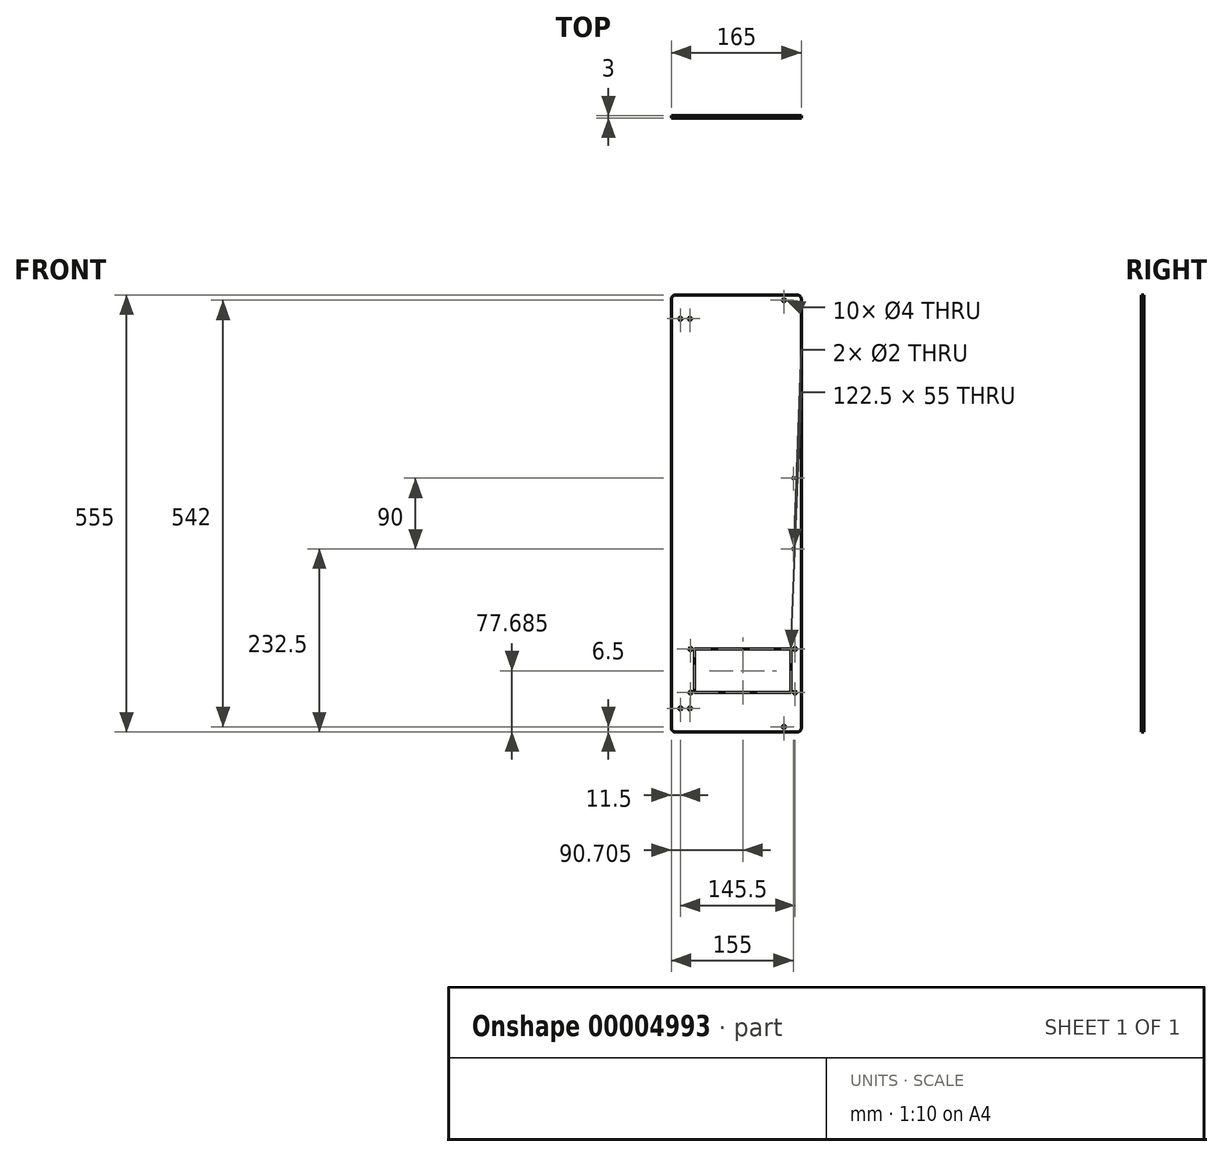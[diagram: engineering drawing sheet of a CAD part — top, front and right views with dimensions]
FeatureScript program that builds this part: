
annotation { "Feature Type Name" : "Feature", "Feature Type Description" : "" }
export const myFeature = defineFeature(function(context is Context, id is Id, definition is map)
    precondition{}
    {
        {
            var Q0;
            Q0=qCreatedBy(makeId("Front.planeOp"),FACE);
            var sketch = newSketch(context, id + "F0", { "sketchPlane" : qUnion([Q0])});
            skLineSegment(sketch, "E0.rect.bottom", {"start": v(82.5, 277.5) * mm, "end": v(-82.5, 277.5) * mm});
            skLineSegment(sketch, "E0.rect.top", {"start": v(82.5, -277.5) * mm, "end": v(-82.5, -277.5) * mm});
            skLineSegment(sketch, "E0.rect.left", {"start": v(82.5, 277.5) * mm, "end": v(82.5, -277.5) * mm});
            skLineSegment(sketch, "E0.rect.right", {"start": v(-82.5, 277.5) * mm, "end": v(-82.5, -277.5) * mm});
            skPoint(sketch, "E0.rect.middle", {"position": v(0, 0) * mm});
            skLineSegment(sketch, "E1", {"start": v(0, 277.5) * mm, "end": v(0, -277.5) * mm, "construction": true});
            skLineSegment(sketch, "E2", {"start": v(0, 0) * mm, "end": v(82.5, 0) * mm, "construction": true});
            skCircle(sketch, "E3", {"center": v(80.17, 273.25) * mm, "radius": 1.5 * mm, "construction": true});
            skCircle(sketch, "E4.0.MirrorC", {"center": v(80.17, -273.25) * mm, "radius": 1.5 * mm, "construction": true});
            skCircle(sketch, "E5.0.MirrorC", {"center": v(-80.17, -273.25) * mm, "radius": 1.5 * mm, "construction": true});
            skCircle(sketch, "E5.1.MirrorC", {"center": v(-80.17, 273.25) * mm, "radius": 1.5 * mm, "construction": true});
            skSolve(sketch);
        }
        {
            var Q0;
            Q0=qSketchRegion(id+"F0",true);
            extrude(context, id + "F1", {"entities" : qUnion([Q0]), "depth" : 3 * mm});
        }
        {
            var Q0;
            Q0=makeQuery(id+"F1.opExtrude","SWEPT_EDGE",EDGE,{"disambiguationData":[OSD([sQuery(id+"F0.wireOp",EDGE,"E0.rect.bottom"),sQuery(id+"F0.wireOp",EDGE,"E0.rect.left")])]});
            var Q1;
            Q1=makeQuery(id+"F1.opExtrude","SWEPT_EDGE",EDGE,{"disambiguationData":[OSD([sQuery(id+"F0.wireOp",EDGE,"E0.rect.bottom"),sQuery(id+"F0.wireOp",EDGE,"E0.rect.right")])]});
            var Q2;
            Q2=makeQuery(id+"F1.opExtrude","SWEPT_EDGE",EDGE,{"disambiguationData":[OSD([sQuery(id+"F0.wireOp",EDGE,"E0.rect.top"),sQuery(id+"F0.wireOp",EDGE,"E0.rect.left")])]});
            var Q3;
            Q3=makeQuery(id+"F1.opExtrude","SWEPT_EDGE",EDGE,{"disambiguationData":[OSD([sQuery(id+"F0.wireOp",EDGE,"E0.rect.top"),sQuery(id+"F0.wireOp",EDGE,"E0.rect.right")])]});
            fillet(context, id + "F2", {"entities" : qUnion([Q0, Q1, Q2, Q3]), "radius" : 5 * mm, "tangentPropagation" : true, "allowEdgeOverflow" : false});
        }
        {
            var Q0;
            Q0=makeQuery(id+"F1.opExtrude","CAP_FACE",FACE,{"disambiguationData":[OSD([sQuery(id+"F0.wireOp",EDGE,"E0.rect.bottom"),sQuery(id+"F0.wireOp",EDGE,"E0.rect.top"),sQuery(id+"F0.wireOp",EDGE,"E0.rect.left"),sQuery(id+"F0.wireOp",EDGE,"E0.rect.right")])],"isStart":false});
            var sketch = newSketch(context, id + "F3", { "sketchPlane" : qUnion([Q0])});
            skLineSegment(sketch, "E6", {"start": v(-82.5, 0) * mm, "end": v(82.5, 0) * mm, "construction": true});
            skLineSegment(sketch, "E7", {"start": v(-82.5, 247.5) * mm, "end": v(82.5, 247.5) * mm, "construction": true});
            skCircle(sketch, "E8", {"center": v(-71, 247.5) * mm, "radius": 2 * mm});
            skCircle(sketch, "E9", {"center": v(-59, 247.5) * mm, "radius": 2 * mm});
            skCircle(sketch, "E10.0.MirrorC", {"center": v(-59, -247.5) * mm, "radius": 2 * mm});
            skCircle(sketch, "E10.1.MirrorC", {"center": v(-71, -247.5) * mm, "radius": 2 * mm});
            skSolve(sketch);
        }
        {
            var Q0;
            Q0=qSketchRegion(id+"F3",true);
            extrude(context, id + "F4", {"entities" : qUnion([Q0]), "operationType" : NewBodyOperationType.REMOVE, "endBound" : BoundingType.THROUGH_ALL, "oppositeDirection" : true, "depth" : 25 * mm});
        }
        {
            var Q0;
            Q0=makeQuery(id+"F1.opExtrude","CAP_FACE",FACE,{"disambiguationData":[OSD([sQuery(id+"F0.wireOp",EDGE,"E0.rect.bottom"),sQuery(id+"F0.wireOp",EDGE,"E0.rect.top"),sQuery(id+"F0.wireOp",EDGE,"E0.rect.left"),sQuery(id+"F0.wireOp",EDGE,"E0.rect.right")])],"isStart":false});
            var sketch = newSketch(context, id + "F5", { "sketchPlane" : qUnion([Q0])});
            skCircle(sketch, "E11", {"center": v(60.5, 271) * mm, "radius": 2 * mm});
            skLineSegment(sketch, "E12", {"start": v(0, 0) * mm, "end": v(139.05, 0) * mm, "construction": true});
            skCircle(sketch, "E13.0.MirrorC", {"center": v(60.5, -271) * mm, "radius": 2 * mm});
            skSolve(sketch);
        }
        {
            var Q0;
            Q0=qSketchRegion(id+"F5",true);
            extrude(context, id + "F6", {"entities" : qUnion([Q0]), "operationType" : NewBodyOperationType.REMOVE, "endBound" : BoundingType.THROUGH_ALL, "oppositeDirection" : true, "depth" : 25 * mm});
        }
        {
            var Q0;
            Q0=makeQuery(id+"F1.opExtrude","CAP_FACE",FACE,{"disambiguationData":[OSD([sQuery(id+"F0.wireOp",EDGE,"E0.rect.bottom"),sQuery(id+"F0.wireOp",EDGE,"E0.rect.top"),sQuery(id+"F0.wireOp",EDGE,"E0.rect.left"),sQuery(id+"F0.wireOp",EDGE,"E0.rect.right")])],"isStart":false});
            var sketch = newSketch(context, id + "F7", { "sketchPlane" : qUnion([Q0])});
            skLineSegment(sketch, "E14", {"start": v(0, 0) * mm, "end": v(84.02, 0) * mm, "construction": true});
            skCircle(sketch, "E15", {"center": v(72.5, 45) * mm, "radius": 1 * mm});
            skCircle(sketch, "E16.0.MirrorC", {"center": v(72.5, -45) * mm, "radius": 1 * mm});
            skSolve(sketch);
        }
        {
            var Q0;
            Q0=qSketchRegion(id+"F7",true);
            extrude(context, id + "F8", {"entities" : qUnion([Q0]), "operationType" : NewBodyOperationType.REMOVE, "endBound" : BoundingType.THROUGH_ALL, "oppositeDirection" : true, "depth" : 25 * mm});
        }
        {
            var Q0;
            Q0=makeQuery(id+"F1.opExtrude","CAP_FACE",FACE,{"disambiguationData":[OSD([sQuery(id+"F0.wireOp",EDGE,"E0.rect.bottom"),sQuery(id+"F0.wireOp",EDGE,"E0.rect.top"),sQuery(id+"F0.wireOp",EDGE,"E0.rect.left"),sQuery(id+"F0.wireOp",EDGE,"E0.rect.right")])],"isStart":false});
            var sketch = newSketch(context, id + "F9", { "sketchPlane" : qUnion([Q0])});
            skLineSegment(sketch, "E17.bottom", {"start": v(-53.05, -172.31) * mm, "end": v(69.45, -172.31) * mm});
            skLineSegment(sketch, "E17.top", {"start": v(-53.05, -227.31) * mm, "end": v(69.45, -227.31) * mm});
            skLineSegment(sketch, "E17.left", {"start": v(-53.05, -172.31) * mm, "end": v(-53.05, -227.31) * mm});
            skLineSegment(sketch, "E17.right", {"start": v(69.45, -172.31) * mm, "end": v(69.45, -227.31) * mm});
            skLineSegment(sketch, "E18", {"start": v(-53.05, -199.81) * mm, "end": v(69.45, -199.81) * mm, "construction": true});
            skLineSegment(sketch, "E19", {"start": v(8.2, -227.31) * mm, "end": v(8.2, -172.31) * mm, "construction": true});
            skCircle(sketch, "E20", {"center": v(-58.1, -172.13) * mm, "radius": 2 * mm});
            skCircle(sketch, "E21.0.MirrorC", {"center": v(74.5, -172.13) * mm, "radius": 2 * mm});
            skCircle(sketch, "E22.0.MirrorC", {"center": v(-58.1, -227.5) * mm, "radius": 2 * mm});
            skCircle(sketch, "E22.1.MirrorC", {"center": v(74.5, -227.5) * mm, "radius": 2 * mm});
            skPoint(sketch, "E23", {"position": v(-59, -247.5) * mm});
            skSolve(sketch);
        }
        {
            var Q0;
            Q0 = qSketchRegion(id + "F9", true);
            extrude(context, id + "F10", {"entities" : qUnion([Q0]), "operationType" : NewBodyOperationType.REMOVE, "endBound" : BoundingType.THROUGH_ALL, "oppositeDirection" : true, "depth" : 25 * mm});
        }
    });
